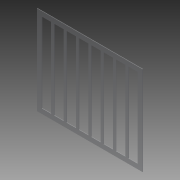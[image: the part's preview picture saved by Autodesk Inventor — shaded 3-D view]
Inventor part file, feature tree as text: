
AUTODESK INVENTOR PART (.ipt)
format: ipt  version: 2013 (Build 170138000, 138)  size: 113,152 bytes
history: native  units: in
note: dims shown in document units (in); Inventor stores cm internally (conversion verified against a paired STEP export)
features: extrude x1, sketch x1
ambient origin geometry x8: Origin, YZ Plane, XZ Plane, XY Plane, X Axis, Y Axis, Z Axis, Center Point
bodies: Solid1 (feature_tree)
feature tree (2):
  extrude  "Extrusion1"  Depth=11.125in
  sketch  "Sketch1"  dims[d0=9.3761in d1=11.125in d2=1.0in d3=0.5in d5=0.5in d6=0.5in d7=3.1496in d9=1.3036in d10=0.3937in d12=1.0in d14=0.0625in d15=0.0in]
